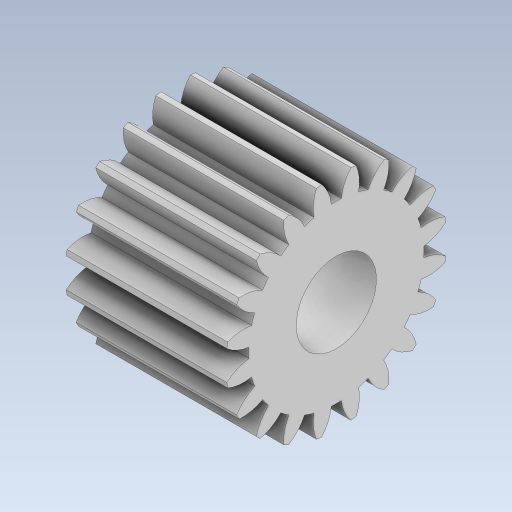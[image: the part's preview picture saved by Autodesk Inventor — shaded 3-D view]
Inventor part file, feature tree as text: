
AUTODESK INVENTOR PART (.ipt)
format: ipt  version: 2023 (Build 270158000, 158)  size: 290,816 bytes
history: native  units: in
note: dims shown in document units (in); Inventor stores cm internally (conversion verified against a paired STEP export)
features: extrude x2, sketch x2, other x1
ambient origin geometry x8: Origin, YZ Plane, XZ Plane, XY Plane, X Axis, Y Axis, Z Axis, Center Point
bodies: Solid1 (feature_tree)
feature tree (5):
  extrude  "Extrusion1"  TaperAngle=0.0deg  [1 undecoded]
  extrude  "Extrusion2"  TaperAngle=0.0deg  [1 undecoded]
  sketch  "Sketch1"  dims[d0=0.5in d1=0.0in d2=0.0in]
  sketch  "Sketch2"  dims[d4=0.25in d5=0.0in d6=0.0in]
  other  "TeethCuts"
note: 2 required parameter values undecoded (feature->parameter linkage not recoverable at this tier; creation-order binding heuristic only, values carry confidence <= 0.55)
